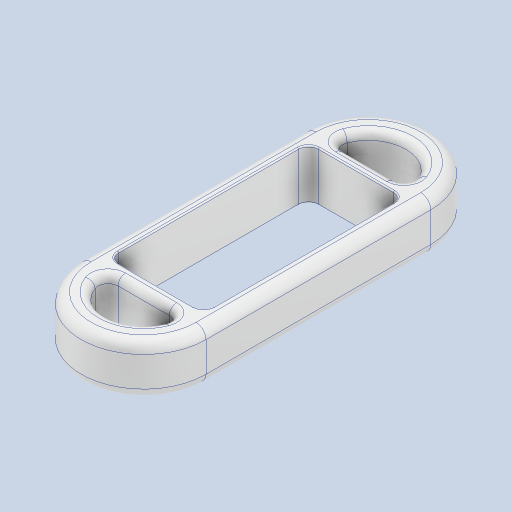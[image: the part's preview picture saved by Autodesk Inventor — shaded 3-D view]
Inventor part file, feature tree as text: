
AUTODESK INVENTOR PART (.ipt)
format: ipt  version: 2024 (Build 280153000, 153)  size: 546,816 bytes
history: native  units: mm
features: fillet x4, extrude x1, sketch x1
ambient origin geometry x8: Origin, YZ Plane, XZ Plane, XY Plane, X Axis, Y Axis, Z Axis, Center Point
bodies: Body1 (feature_tree)
feature tree (6):
  extrude  "Extrusión2"  Depth=10.0mm
  fillet  "Empalme2"  Radius=80.0mm
  fillet  "Empalme3"  Radius=38.0mm
  fillet  "Empalme4"  Radius=20.0mm
  fillet  "Empalme5"  Radius=4.0mm
  sketch  "Boceto1"  dims[d1=50.0mm d3=10.0mm d11=80.0mm d12=38.0mm d13=20.0mm d14=0.0mm d15=4.0mm d16=4.0mm d18=6.0mm d19=3.0mm d20=0.5mm]
